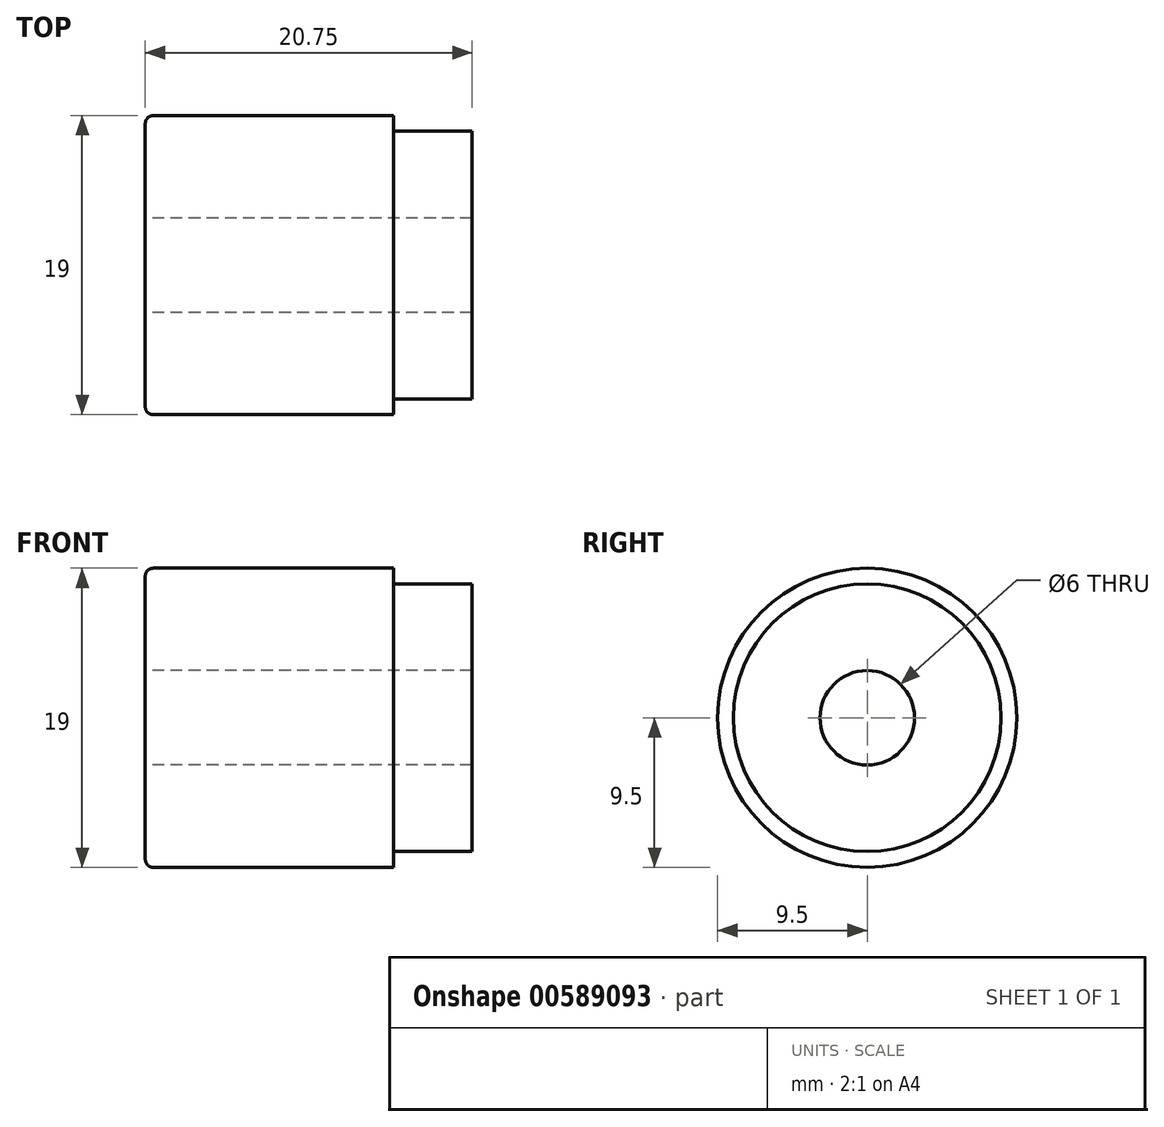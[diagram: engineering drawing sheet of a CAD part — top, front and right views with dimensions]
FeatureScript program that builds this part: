
annotation { "Feature Type Name" : "Feature", "Feature Type Description" : "" }
export const myFeature = defineFeature(function(context is Context, id is Id, definition is map)
    precondition{}
    {
        {
            var Q0;
            Q0=qCreatedBy(makeId("Front.planeOp"),FACE);
            var sketch = newSketch(context, id + "F0", { "sketchPlane" : qUnion([Q0])});
            skLineSegment(sketch, "E0.bottom", {"start": v(-15.25, 9.5) * mm, "end": v(0, 9.5) * mm});
            skLineSegment(sketch, "E0.top", {"start": v(-15.75, 0) * mm, "end": v(5, 0) * mm, "construction": true});
            skLineSegment(sketch, "E0.left", {"start": v(-15.75, 9) * mm, "end": v(-15.75, 3) * mm});
            skLineSegment(sketch, "E0.right", {"start": v(5, 8.5) * mm, "end": v(5, 3) * mm});
            skLineSegment(sketch, "E1", {"start": v(5, 8.5) * mm, "end": v(0, 8.5) * mm});
            skLineSegment(sketch, "E2", {"start": v(0, 8.5) * mm, "end": v(0, 9.5) * mm});
            skPoint(sketch, "E3.visualSharp", {"position": v(-15.75, 9.5) * mm});
            skArc(sketch, "E3.filletArc", {"start": v(-15.25, 9.5) * mm, "mid": v(-15.6, 9.35) * mm, "end": v(-15.75, 9) * mm});
            skLineSegment(sketch, "E4", {"start": v(-15.75, 3) * mm, "end": v(5, 3) * mm});
            skSolve(sketch);
        }
        {
            var Q0;
            Q0 = qSketchRegion(id + "F0", true);
            var Q1;
            Q1=sQuery(id+"F0.wireOp",EDGE,"E0.top");
            revolve(context, id + "F1", {"entities" : qUnion([Q0]), "axis" : qUnion([Q1]), "revolveType" : RevolveType.FULL});
        }
    });
